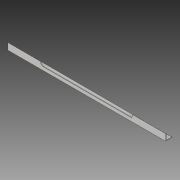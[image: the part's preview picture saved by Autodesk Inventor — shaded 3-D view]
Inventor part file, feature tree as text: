
AUTODESK INVENTOR PART (.ipt)
format: ipt  version: 2018 (Build 220112000, 112)  size: 94,720 bytes
history: native  units: in
note: dims shown in document units (in); Inventor stores cm internally (conversion verified against a paired STEP export)
features: fillet x1
ambient origin geometry x8: Origin, YZ Plane, XZ Plane, XY Plane, X Axis, Y Axis, Z Axis, Center Point
bodies: Solid1 (feature_tree)
feature tree (1):
  fillet  "Fillet1"  [1 undecoded]
note: 1 required parameter value undecoded (feature->parameter linkage not recoverable at this tier; creation-order binding heuristic only, values carry confidence <= 0.55)
